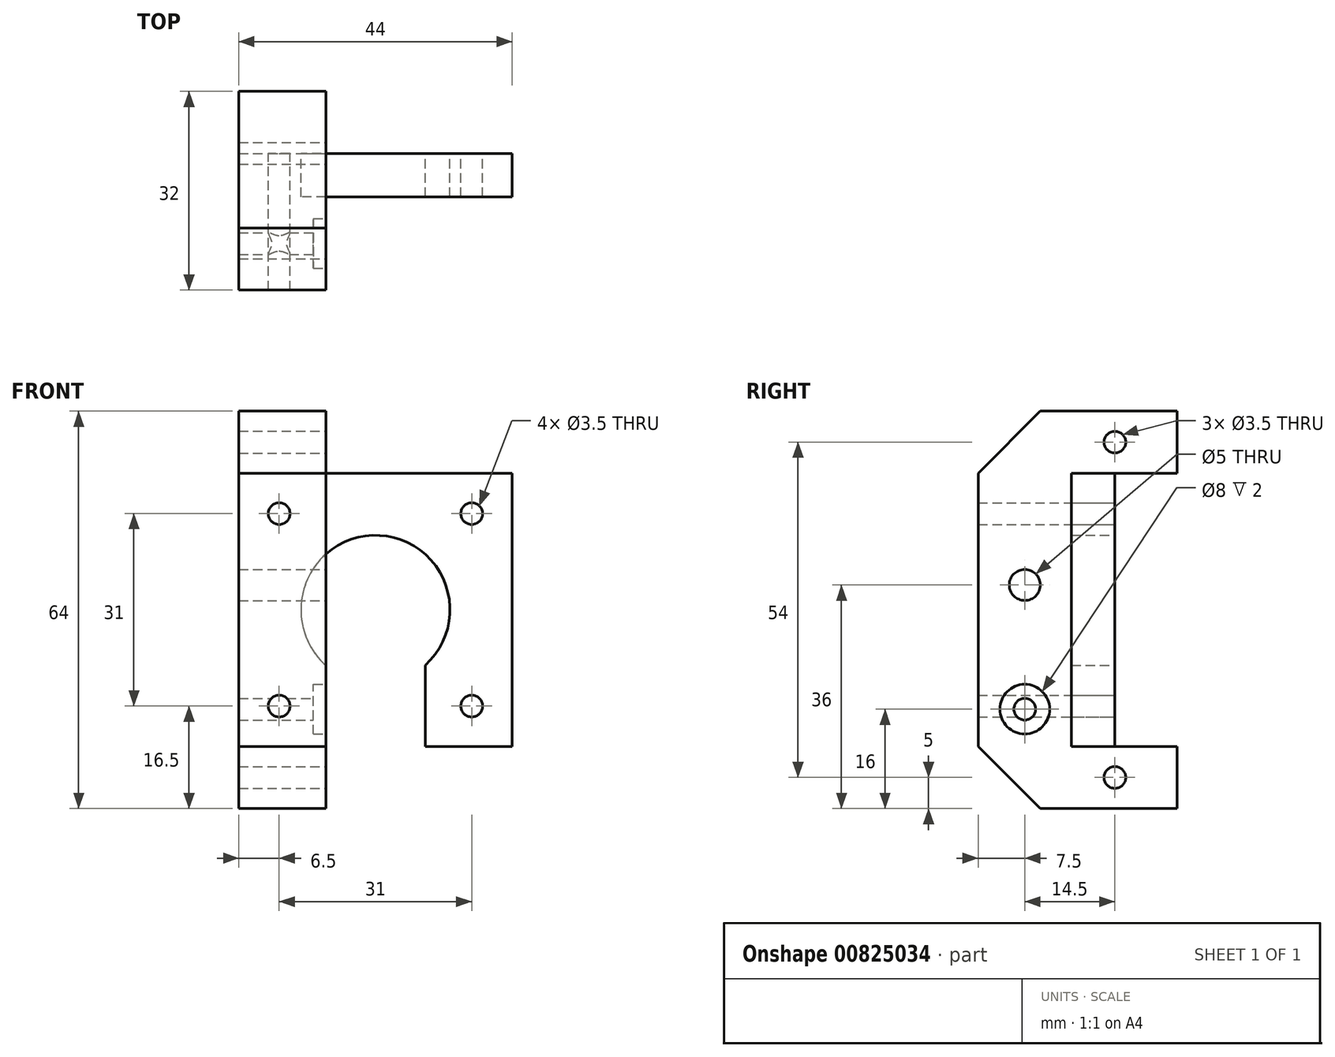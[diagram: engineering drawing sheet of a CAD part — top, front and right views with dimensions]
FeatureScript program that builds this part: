
annotation { "Feature Type Name" : "Feature", "Feature Type Description" : "" }
export const myFeature = defineFeature(function(context is Context, id is Id, definition is map)
    precondition{}
    {
        {
            var Q0;
            Q0=qCreatedBy(makeId("Front.planeOp"),FACE);
            var sketch = newSketch(context, id + "F0", { "sketchPlane" : qUnion([Q0])});
            skLineSegment(sketch, "E0.bottom", {"start": v(0, 0) * mm, "end": v(14, 0) * mm});
            skLineSegment(sketch, "E0.top", {"start": v(0, 44) * mm, "end": v(44, 44) * mm});
            skLineSegment(sketch, "E0.left", {"start": v(0, 0) * mm, "end": v(0, 44) * mm});
            skLineSegment(sketch, "E0.right", {"start": v(44, 0) * mm, "end": v(44, 44) * mm});
            skPoint(sketch, "E1.oppositeSnap0", {"position": v(0, 22) * mm});
            skArc(sketch, "E2", {"start": v(30, 13.06) * mm, "mid": v(22, 34) * mm, "end": v(14, 13.06) * mm});
            skPoint(sketch, "E2.centerSnap0", {"position": v(22, 0) * mm});
            skCircle(sketch, "E3", {"center": v(6.5, 37.5) * mm, "radius": 1.75 * mm});
            skCircle(sketch, "E4", {"center": v(37.5, 37.5) * mm, "radius": 1.75 * mm});
            skCircle(sketch, "E5", {"center": v(37.5, 6.5) * mm, "radius": 1.75 * mm});
            skCircle(sketch, "E6", {"center": v(6.5, 6.5) * mm, "radius": 1.75 * mm});
            skLineSegment(sketch, "E7", {"start": v(14, 0) * mm, "end": v(14, 13.06) * mm});
            skLineSegment(sketch, "E8", {"start": v(30, 0) * mm, "end": v(30, 13.06) * mm});
            skLineSegment(sketch, "E9.trimOffspring", {"start": v(30, 0) * mm, "end": v(44, 0) * mm});
            skSolve(sketch);
        }
        {
            var Q0;
            Q0 = qSketchRegion(id + "F0", true);
            extrude(context, id + "F1", {"entities" : qUnion([Q0]), "depth" : 7 * mm, "offsetDistance" : 25 * mm});
        }
        {
            var Q0;
            Q0=makeQuery(id+"F1.opExtrude","CAP_FACE",FACE,{"disambiguationData":[OSD([sQuery(id+"F0.wireOp",EDGE,"E0.bottom"),sQuery(id+"F0.wireOp",EDGE,"E0.top"),sQuery(id+"F0.wireOp",EDGE,"E0.left"),sQuery(id+"F0.wireOp",EDGE,"E0.right"),sQuery(id+"F0.wireOp",EDGE,"E2"),sQuery(id+"F0.wireOp",EDGE,"E3"),sQuery(id+"F0.wireOp",EDGE,"E4"),sQuery(id+"F0.wireOp",EDGE,"E5"),sQuery(id+"F0.wireOp",EDGE,"E6"),sQuery(id+"F0.wireOp",EDGE,"E7"),sQuery(id+"F0.wireOp",EDGE,"E8"),sQuery(id+"F0.wireOp",EDGE,"E9.trimOffspring")])],"isStart":false});
            var sketch = newSketch(context, id + "F2", { "sketchPlane" : qUnion([Q0])});
            skLineSegment(sketch, "E10.bottom", {"start": v(0, 44) * mm, "end": v(14, 44) * mm});
            skLineSegment(sketch, "E10.top", {"start": v(0, 0) * mm, "end": v(14, 0) * mm});
            skLineSegment(sketch, "E10.left", {"start": v(0, 44) * mm, "end": v(0, 0) * mm});
            skLineSegment(sketch, "E10.right", {"start": v(14, 44) * mm, "end": v(14, 0) * mm});
            skCircle(sketch, "E11", {"center": v(6.5, 37.5) * mm, "radius": 1.75 * mm});
            skCircle(sketch, "E12", {"center": v(6.5, 6.5) * mm, "radius": 1.75 * mm});
            skCircle(sketch, "E13", {"center": v(22, 22) * mm, "radius": 2 * mm, "construction": true});
            skCircle(sketch, "E14", {"center": v(22, 30.5) * mm, "radius": 6.5 * mm, "construction": true});
            skSolve(sketch);
        }
        {
            var Q0;
            Q0 = qSketchRegion(id + "F2", true);
            extrude(context, id + "F3", {"entities" : qUnion([Q0]), "operationType" : NewBodyOperationType.ADD, "depth" : 15 * mm, "offsetDistance" : 25 * mm});
        }
        {
            var Q0;
            Q0=makeQuery(id+"F3.boolean.opBoolean","MERGE",FACE,{"derivedFrom":[makeQuery(id+"F1.opExtrude","SWEPT_FACE",FACE,{"disambiguationData":[OSD([sQuery(id+"F0.wireOp",EDGE,"E7")])]}),makeQuery(id+"F3.opExtrude","SWEPT_FACE",FACE,{"disambiguationData":[OSD([sQuery(id+"F2.wireOp",EDGE,"E10.right")])]})]});
            var sketch = newSketch(context, id + "F4", { "sketchPlane" : qUnion([Q0])});
            skCircle(sketch, "E15", {"center": v(-14.5, 26) * mm, "radius": 2.5 * mm});
            skCircle(sketch, "E16", {"center": v(-14.5, 6) * mm, "radius": 1.75 * mm});
            skSolve(sketch);
        }
        {
            var Q0;
            Q0 = qSketchRegion(id + "F4", true);
            extrude(context, id + "F5", {"entities" : qUnion([Q0]), "operationType" : NewBodyOperationType.REMOVE, "oppositeDirection" : true, "depth" : 25 * mm, "offsetDistance" : 25 * mm});
        }
        {
            var Q0;
            Q0=makeQuery(id+"F3.boolean.opBoolean","MERGE",FACE,{"derivedFrom":[makeQuery(id+"F1.opExtrude","SWEPT_FACE",FACE,{"disambiguationData":[OSD([sQuery(id+"F0.wireOp",EDGE,"E7")])]}),makeQuery(id+"F3.opExtrude","SWEPT_FACE",FACE,{"disambiguationData":[OSD([sQuery(id+"F2.wireOp",EDGE,"E10.right")])]})]});
            var sketch = newSketch(context, id + "F6", { "sketchPlane" : qUnion([Q0])});
            skCircle(sketch, "E17", {"center": v(-14.5, 6) * mm, "radius": 4 * mm});
            skSolve(sketch);
        }
        {
            var Q0;
            Q0 = qSketchRegion(id + "F6", true);
            extrude(context, id + "F7", {"entities" : qUnion([Q0]), "operationType" : NewBodyOperationType.REMOVE, "oppositeDirection" : true, "depth" : 2 * mm, "offsetDistance" : 25 * mm});
        }
        {
            var Q0;
            Q0=makeQuery(id+"F3.boolean.opBoolean","MERGE",FACE,{"derivedFrom":[makeQuery(id+"F1.opExtrude","SWEPT_FACE",FACE,{"disambiguationData":[OSD([sQuery(id+"F0.wireOp",EDGE,"E0.top")])]}),makeQuery(id+"F3.opExtrude","SWEPT_FACE",FACE,{"disambiguationData":[OSD([sQuery(id+"F2.wireOp",EDGE,"E10.bottom")])]})]});
            var sketch = newSketch(context, id + "F8", { "sketchPlane" : qUnion([Q0])});
            skLineSegment(sketch, "E18.bottom", {"start": v(0, -22) * mm, "end": v(14, -22) * mm});
            skLineSegment(sketch, "E18.top", {"start": v(0, 10) * mm, "end": v(14, 10) * mm});
            skLineSegment(sketch, "E18.left", {"start": v(0, -22) * mm, "end": v(0, 10) * mm});
            skLineSegment(sketch, "E18.right", {"start": v(14, -22) * mm, "end": v(14, 10) * mm});
            skSolve(sketch);
        }
        {
            var Q0;
            Q0 = qSketchRegion(id + "F8", true);
            extrude(context, id + "F9", {"entities" : qUnion([Q0]), "operationType" : NewBodyOperationType.ADD, "depth" : 10 * mm, "offsetDistance" : 25 * mm});
        }
        {
            var Q0;
            Q0=makeQuery(id+"F3.boolean.opBoolean","MERGE",FACE,{"derivedFrom":[makeQuery(id+"F1.opExtrude","SWEPT_FACE",FACE,{"disambiguationData":[OSD([sQuery(id+"F0.wireOp",EDGE,"E0.bottom")])]}),makeQuery(id+"F3.opExtrude","SWEPT_FACE",FACE,{"disambiguationData":[OSD([sQuery(id+"F2.wireOp",EDGE,"E10.top")])]})]});
            var sketch = newSketch(context, id + "F10", { "sketchPlane" : qUnion([Q0])});
            skLineSegment(sketch, "E19.bottom", {"start": v(0, 22) * mm, "end": v(14, 22) * mm});
            skLineSegment(sketch, "E19.top", {"start": v(0, -10) * mm, "end": v(14, -10) * mm});
            skLineSegment(sketch, "E19.left", {"start": v(0, 22) * mm, "end": v(0, -10) * mm});
            skLineSegment(sketch, "E19.right", {"start": v(14, 22) * mm, "end": v(14, -10) * mm});
            skSolve(sketch);
        }
        {
            var Q0;
            Q0 = qSketchRegion(id + "F10", true);
            extrude(context, id + "F11", {"entities" : qUnion([Q0]), "operationType" : NewBodyOperationType.ADD, "depth" : 10 * mm, "offsetDistance" : 25 * mm});
        }
        {
            var Q0;
            Q0=makeQuery(id+"F11.boolean.opBoolean","MERGE",FACE,{"derivedFrom":[makeQuery(id+"F9.boolean.opBoolean","MERGE",FACE,{"derivedFrom":[makeQuery(id+"F3.boolean.opBoolean","MERGE",FACE,{"derivedFrom":[makeQuery(id+"F1.opExtrude","SWEPT_FACE",FACE,{"disambiguationData":[OSD([sQuery(id+"F0.wireOp",EDGE,"E7")])]}),makeQuery(id+"F3.opExtrude","SWEPT_FACE",FACE,{"disambiguationData":[OSD([sQuery(id+"F2.wireOp",EDGE,"E10.right")])]})]}),makeQuery(id+"F9.opExtrude","SWEPT_FACE",FACE,{"disambiguationData":[OSD([sQuery(id+"F8.wireOp",EDGE,"E18.right")])]})]}),makeQuery(id+"F11.opExtrude","SWEPT_FACE",FACE,{"disambiguationData":[OSD([sQuery(id+"F10.wireOp",EDGE,"E19.right")])]})]});
            var sketch = newSketch(context, id + "F12", { "sketchPlane" : qUnion([Q0])});
            skCircle(sketch, "E20", {"center": v(0, 49) * mm, "radius": 1.75 * mm});
            skCircle(sketch, "E21", {"center": v(0, -5) * mm, "radius": 1.75 * mm});
            skSolve(sketch);
        }
        {
            var Q0;
            Q0 = qSketchRegion(id + "F12", true);
            extrude(context, id + "F13", {"entities" : qUnion([Q0]), "operationType" : NewBodyOperationType.REMOVE, "oppositeDirection" : true, "depth" : 25 * mm, "offsetDistance" : 25 * mm});
        }
        {
            var Q0;
            Q0=makeQuery(id+"F9.opExtrude","CAP_EDGE",EDGE,{"disambiguationData":[OSD([sQuery(id+"F8.wireOp",EDGE,"E18.bottom")])],"isStart":false});
            var Q1;
            Q1=makeQuery(id+"F11.opExtrude","CAP_EDGE",EDGE,{"disambiguationData":[OSD([sQuery(id+"F10.wireOp",EDGE,"E19.bottom")])],"isStart":false});
            chamfer(context, id + "F14", {"entities" : qUnion([Q0, Q1]), "width" : 10 * mm, "tangentPropagation" : true});
        }
    });
